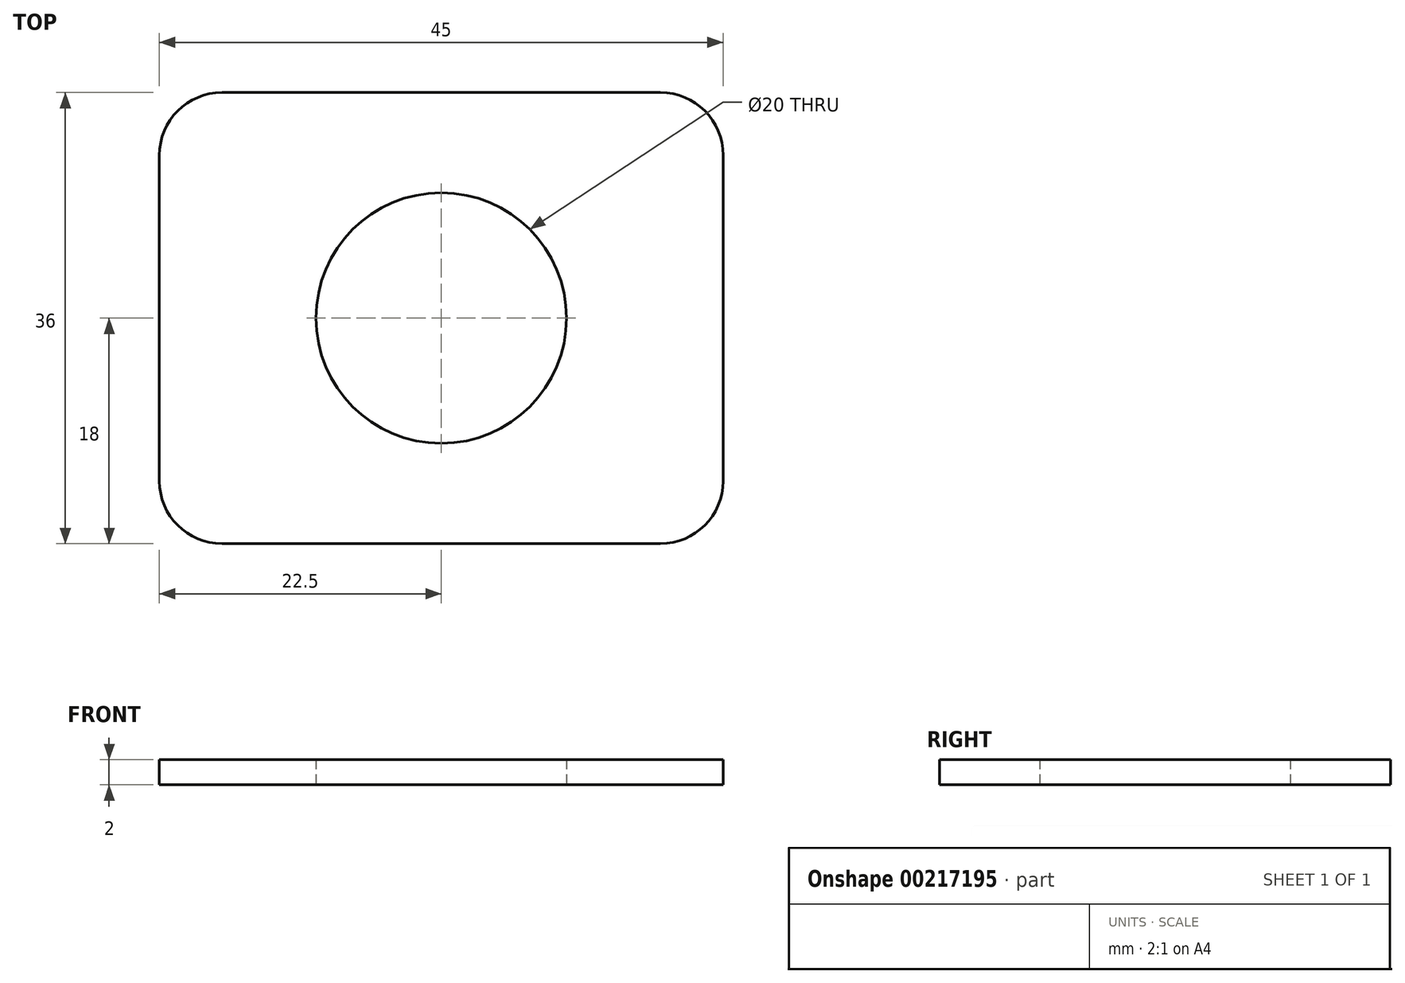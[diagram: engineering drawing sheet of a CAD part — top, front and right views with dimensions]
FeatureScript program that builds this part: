
annotation { "Feature Type Name" : "Feature", "Feature Type Description" : "" }
export const myFeature = defineFeature(function(context is Context, id is Id, definition is map)
    precondition{}
    {
        {
            var Q0;
            Q0=qCreatedBy(makeId("Top.planeOp"),FACE);
            var sketch = newSketch(context, id + "F0", { "sketchPlane" : qUnion([Q0])});
            skLineSegment(sketch, "E0.bottom", {"start": v(17.5, 18) * mm, "end": v(-17.5, 18) * mm});
            skLineSegment(sketch, "E0.top", {"start": v(17.5, -18) * mm, "end": v(-17.5, -18) * mm});
            skLineSegment(sketch, "E0.left", {"start": v(22.5, 13) * mm, "end": v(22.5, -13) * mm});
            skLineSegment(sketch, "E0.right", {"start": v(-22.5, 13) * mm, "end": v(-22.5, -13) * mm});
            skPoint(sketch, "E0.middle", {"position": v(0, 0) * mm});
            skPoint(sketch, "E1.visualSharp", {"position": v(-22.5, 18) * mm});
            skArc(sketch, "E1.filletArc", {"start": v(-17.5, 18) * mm, "mid": v(-21.04, 16.54) * mm, "end": v(-22.5, 13) * mm});
            skPoint(sketch, "E2.visualSharp", {"position": v(22.5, 18) * mm});
            skArc(sketch, "E2.filletArc", {"start": v(22.5, 13) * mm, "mid": v(21.04, 16.54) * mm, "end": v(17.5, 18) * mm});
            skPoint(sketch, "E3.visualSharp", {"position": v(22.5, -18) * mm});
            skArc(sketch, "E3.filletArc", {"start": v(17.5, -18) * mm, "mid": v(21.04, -16.54) * mm, "end": v(22.5, -13) * mm});
            skPoint(sketch, "E4.visualSharp", {"position": v(-22.5, -18) * mm});
            skArc(sketch, "E4.filletArc", {"start": v(-22.5, -13) * mm, "mid": v(-21.04, -16.54) * mm, "end": v(-17.5, -18) * mm});
            skCircle(sketch, "E5", {"center": v(0, 0) * mm, "radius": 10 * mm});
            skSolve(sketch);
        }
        {
            var Q0;
            Q0 = qSketchRegion(id + "F0", true);
            extrude(context, id + "F1", {"entities" : qUnion([Q0]), "depth" : 2 * mm});
        }
    });
